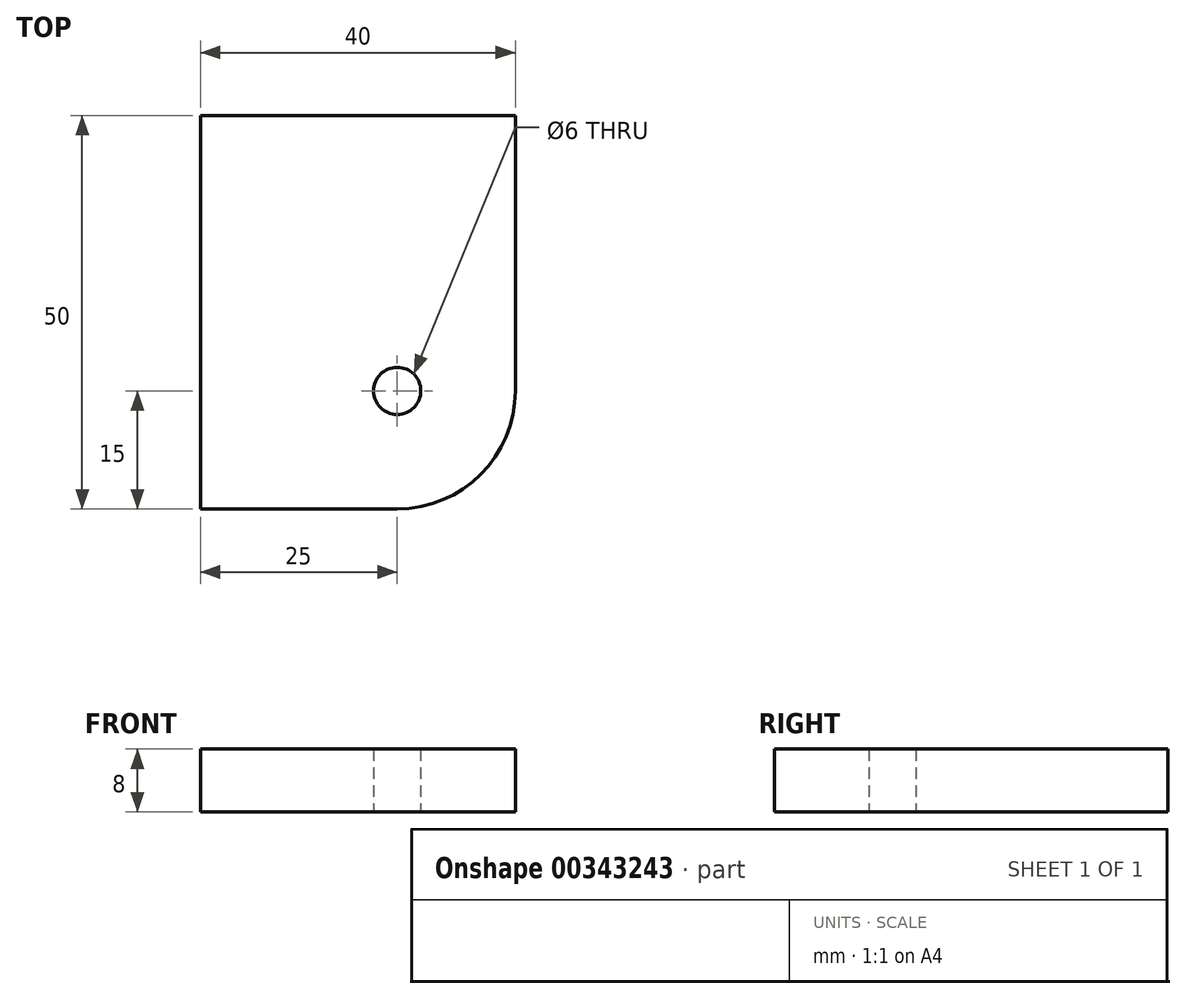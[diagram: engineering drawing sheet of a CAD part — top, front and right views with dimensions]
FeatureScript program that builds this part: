
annotation { "Feature Type Name" : "Feature", "Feature Type Description" : "" }
export const myFeature = defineFeature(function(context is Context, id is Id, definition is map)
    precondition{}
    {
        {
            var Q0;
            Q0=qCreatedBy(makeId("Top.planeOp"),FACE);
            var sketch = newSketch(context, id + "F0", { "sketchPlane" : qUnion([Q0])});
            skLineSegment(sketch, "E0.bottom", {"start": v(15, 25) * mm, "end": v(-15, 25) * mm});
            skLineSegment(sketch, "E0.top", {"start": v(15, -25) * mm, "end": v(-15, -25) * mm});
            skLineSegment(sketch, "E0.left", {"start": v(15, 25) * mm, "end": v(15, -25) * mm});
            skPoint(sketch, "E0.middle", {"position": v(0, 0) * mm});
            skLineSegment(sketch, "E1.0", {"start": v(0, 25) * mm, "end": v(0, -22) * mm, "construction": true});
            skLineSegment(sketch, "E2.0", {"start": v(15, -10) * mm, "end": v(-15, -10) * mm, "construction": true});
            skPoint(sketch, "E3", {"position": v(0, -10) * mm});
            skArc(sketch, "E4", {"start": v(0, -25) * mm, "mid": v(10.6, -20.6) * mm, "end": v(15, -10) * mm});
            skLineSegment(sketch, "E5.0", {"start": v(-25, 25) * mm, "end": v(-25, -25) * mm});
            skLineSegment(sketch, "E6", {"start": v(-25, 25) * mm, "end": v(-15, 25) * mm});
            skLineSegment(sketch, "E7", {"start": v(-25, -25) * mm, "end": v(-15, -25) * mm});
            skSolve(sketch);
        }
        {
            var Q0;
            Q0=makeQuery(id+"F0.imprint","IMPRINT",FACE,{"disambiguationData":[TD([[makeQuery(id+"F0.imprint","IMPRINT",EDGE,{"derivedFrom":sQuery(id+"F0.wireOp",EDGE,"E0.bottom")}),1.0]])]});
            extrude(context, id + "F1", {"entities" : qUnion([Q0]), "depth" : 8 * mm});
        }
        {
            var Q0;
            Q0=sQuery(id+"F0.wireOp",VERTEX,"E3");
            var Q1;
            Q1=makeQuery(id+"F1.opExtrude","SWEPT_BODY",BODY,{"disambiguationData":[OSD([sQuery(id+"F0.wireOp",EDGE,"E0.bottom"),sQuery(id+"F0.wireOp",EDGE,"E0.top"),sQuery(id+"F0.wireOp",EDGE,"E0.left"),sQuery(id+"F0.wireOp",EDGE,"E0.right")])]});
            hole(context, id + "F2", {"style" : HoleStyle.SIMPLE, "endStyle" : HoleEndStyle.THROUGH, "oppositeDirection" : true, "holeDiameter" : 6 * mm, "isTappedThrough" : true, "tappedDepth" : 6 * mm, "tapClearance" : 3, "startFromSketch" : true, "locations" : qUnion([Q0]), "scope" : qUnion([Q1])});
        }
    });
